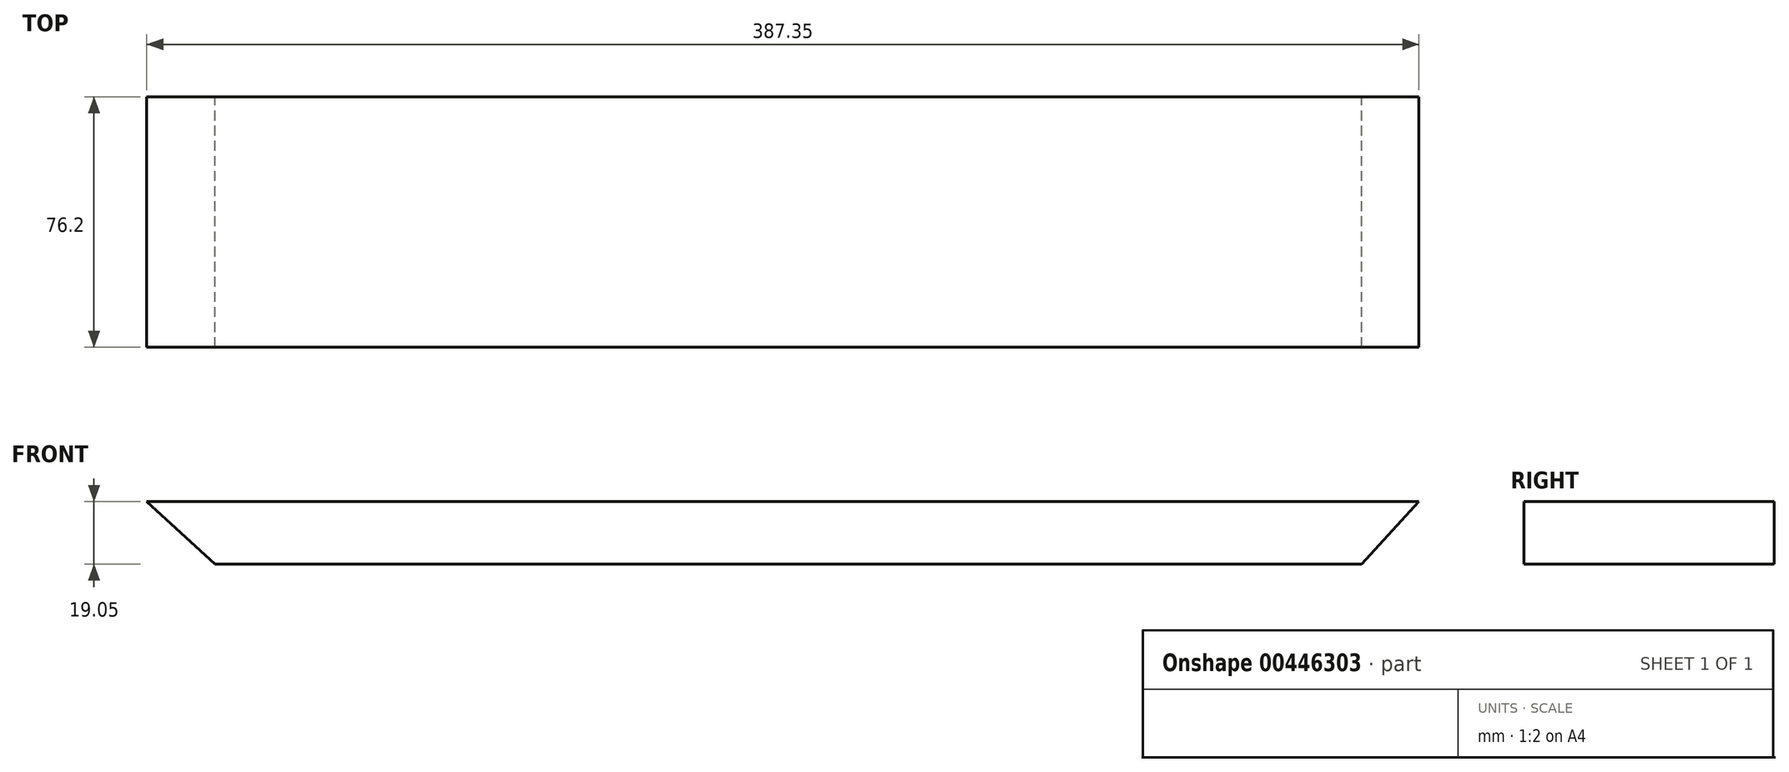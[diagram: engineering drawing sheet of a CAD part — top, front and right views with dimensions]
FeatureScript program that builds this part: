
annotation { "Feature Type Name" : "Feature", "Feature Type Description" : "" }
export const myFeature = defineFeature(function(context is Context, id is Id, definition is map)
    precondition{}
    {
        {
            var Q0;
            Q0=qCreatedBy(makeId("Front.planeOp"),FACE);
            var sketch = newSketch(context, id + "F0", { "sketchPlane" : qUnion([Q0])});
            skLineSegment(sketch, "E0", {"start": v(0, 0) * mm, "end": v(387.35, 0) * mm});
            skLineSegment(sketch, "E1", {"start": v(387.35, 0) * mm, "end": v(369.9, -19.05) * mm});
            skLineSegment(sketch, "E2", {"start": v(369.9, -19.05) * mm, "end": v(20.79, -19.05) * mm});
            skLineSegment(sketch, "E3", {"start": v(20.79, -19.05) * mm, "end": v(0, 0) * mm});
            skSolve(sketch);
        }
        {
            var Q0;
            Q0=makeQuery(id+"F0.imprint","IMPRINT",FACE,{"disambiguationData":[TD([[makeQuery(id+"F0.imprint","IMPRINT",EDGE,{"derivedFrom":sQuery(id+"F0.wireOp",EDGE,"E0")}),-1.0]])]});
            extrude(context, id + "F1", {"entities" : qUnion([Q0]), "depth" : 76.2 * mm});
        }
    });
